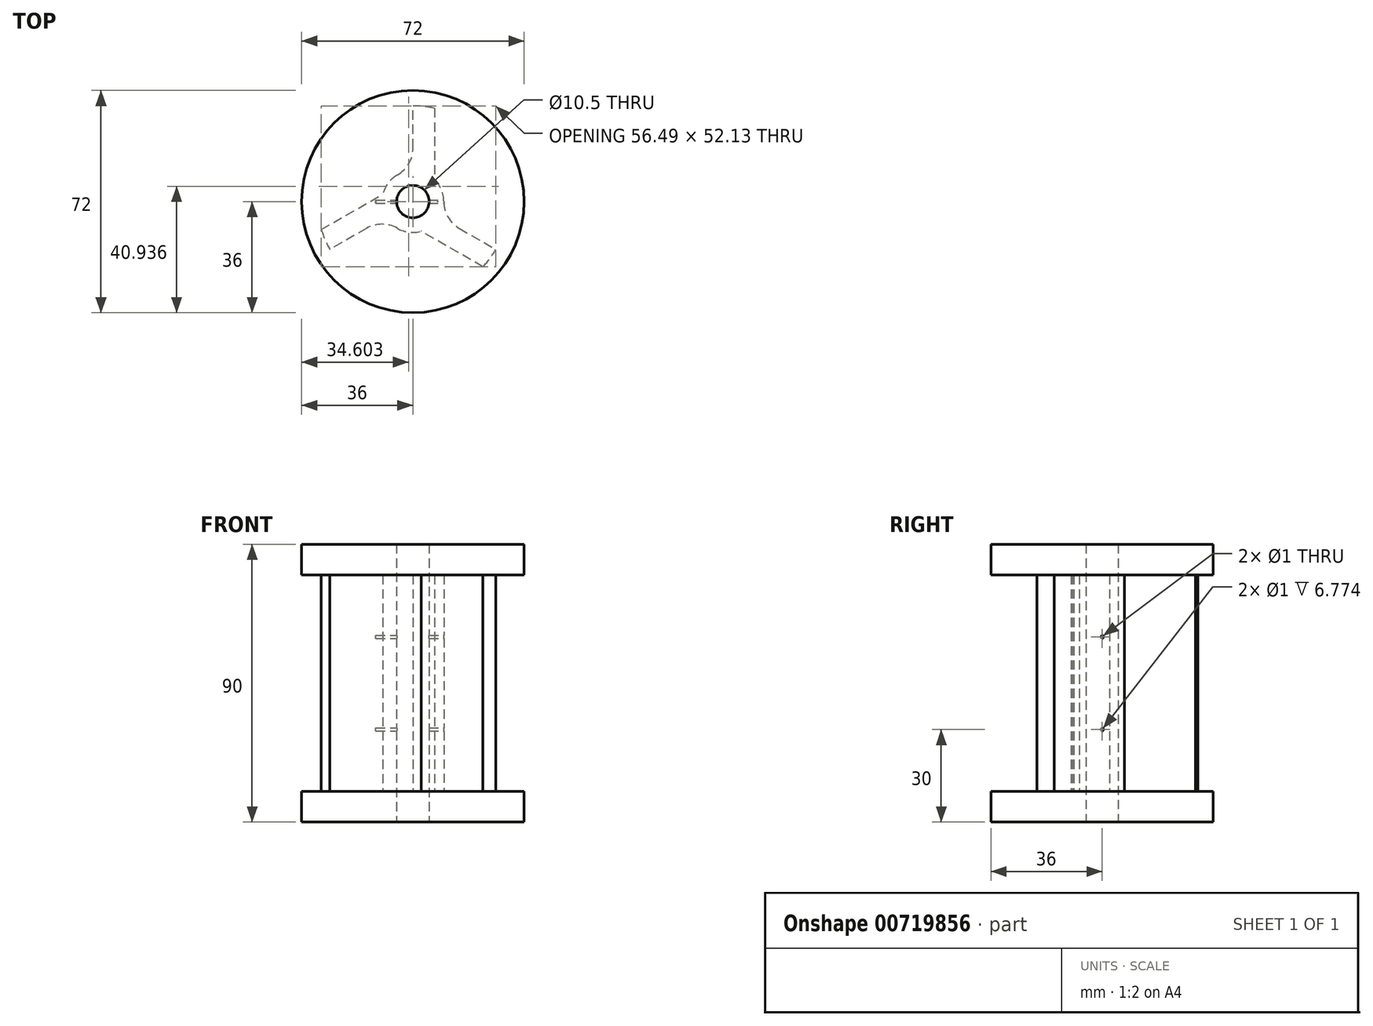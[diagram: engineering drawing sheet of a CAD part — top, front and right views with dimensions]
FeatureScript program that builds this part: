
annotation { "Feature Type Name" : "Feature", "Feature Type Description" : "" }
export const myFeature = defineFeature(function(context is Context, id is Id, definition is map)
    precondition{}
    {
        {
            var Q0;
            Q0=qCreatedBy(makeId("Top.planeOp"),FACE);
            var sketch = newSketch(context, id + "F0", { "sketchPlane" : qUnion([Q0])});
            skCircle(sketch, "E0", {"center": v(0, 0) * mm, "radius": 31 * mm});
            skCircle(sketch, "E1", {"center": v(0, 0) * mm, "radius": 5.25 * mm});
            skCircle(sketch, "E2", {"center": v(0, 0) * mm, "radius": 10 * mm});
            skLineSegment(sketch, "E3", {"start": v(0, 0) * mm, "end": v(-26.85, -15.5) * mm});
            skLineSegment(sketch, "E4", {"start": v(0, 0) * mm, "end": v(0, 31) * mm});
            skLineSegment(sketch, "E5", {"start": v(0, 0) * mm, "end": v(26.85, -15.5) * mm});
            skLineSegment(sketch, "E6", {"start": v(0, 0) * mm, "end": v(-29.64, -9.08) * mm});
            skLineSegment(sketch, "E7", {"start": v(-29.64, -9.08) * mm, "end": v(-9.7, 2.43) * mm});
            skLineSegment(sketch, "E8", {"start": v(0, 0) * mm, "end": v(6.96, 30.2) * mm});
            skLineSegment(sketch, "E9", {"start": v(6.96, 30.2) * mm, "end": v(6.96, 7.19) * mm});
            skLineSegment(sketch, "E10", {"start": v(0, 0) * mm, "end": v(22.68, -21.13) * mm});
            skLineSegment(sketch, "E11", {"start": v(22.68, -21.13) * mm, "end": v(2.74, -9.62) * mm});
            skSolve(sketch);
        }
        {
            var Q0;
            {var subQ3=sQuery(id+"F0.wireOp",EDGE,"E10");var subQ5=sQuery(id+"F0.wireOp",EDGE,"E2");var subQ6=makeQuery(id+"F0.imprint","INTERSECT",VERTEX,{"derivedFrom":[subQ5,subQ3]});Q0=makeQuery(id+"F0.imprint","IMPRINT",FACE,{"disambiguationData":[TD([[makeQuery(id+"F0.imprint","IMPRINT",EDGE,{"disambiguationData":[TD([[subQ6,-1.0]])],"derivedFrom":subQ5}),-1.0]])]});}
            var Q1;
            {var subQ0=sQuery(id+"F0.wireOp",EDGE,"E11");Q1=makeQuery(id+"F0.imprint","IMPRINT",FACE,{"disambiguationData":[TD([[makeQuery(id+"F0.imprint","IMPRINT",EDGE,{"derivedFrom":subQ0}),-1.0]])]});}
            var Q2;
            {var subQ4=sQuery(id+"F0.wireOp",EDGE,"E3");var subQ5=sQuery(id+"F0.wireOp",EDGE,"E1");var subQ6=makeQuery(id+"F0.imprint","INTERSECT",VERTEX,{"derivedFrom":[subQ5,subQ4]});Q2=makeQuery(id+"F0.imprint","IMPRINT",FACE,{"disambiguationData":[TD([[makeQuery(id+"F0.imprint","IMPRINT",EDGE,{"disambiguationData":[TD([[subQ6,-1.0]])],"derivedFrom":subQ5}),-1.0]])]});}
            var Q3;
            {var subQ0=sQuery(id+"F0.wireOp",EDGE,"E10");var subQ1=sQuery(id+"F0.wireOp",EDGE,"E1");var subQ2=makeQuery(id+"F0.imprint","INTERSECT",VERTEX,{"derivedFrom":[subQ1,subQ0]});Q3=makeQuery(id+"F0.imprint","IMPRINT",FACE,{"disambiguationData":[TD([[makeQuery(id+"F0.imprint","IMPRINT",EDGE,{"disambiguationData":[TD([[subQ2,-1.0]])],"derivedFrom":subQ1}),-1.0]])]});}
            var Q4;
            {var subQ1=sQuery(id+"F0.wireOp",EDGE,"E1");var subQ6=sQuery(id+"F0.wireOp",EDGE,"E8");var subQ8=makeQuery(id+"F0.imprint","INTERSECT",VERTEX,{"derivedFrom":[subQ1,subQ6]});Q4=makeQuery(id+"F0.imprint","IMPRINT",FACE,{"disambiguationData":[TD([[makeQuery(id+"F0.imprint","IMPRINT",EDGE,{"disambiguationData":[TD([[subQ8,1.0]])],"derivedFrom":subQ1}),-1.0]])]});}
            var Q5;
            {var subQ0=sQuery(id+"F0.wireOp",EDGE,"E4");var subQ1=sQuery(id+"F0.wireOp",EDGE,"E1");var subQ2=makeQuery(id+"F0.imprint","INTERSECT",VERTEX,{"derivedFrom":[subQ1,subQ0]});Q5=makeQuery(id+"F0.imprint","IMPRINT",FACE,{"disambiguationData":[TD([[makeQuery(id+"F0.imprint","IMPRINT",EDGE,{"disambiguationData":[TD([[subQ2,-1.0]])],"derivedFrom":subQ1}),-1.0]])]});}
            var Q6;
            {var subQ0=sQuery(id+"F0.wireOp",EDGE,"E4");var subQ1=sQuery(id+"F0.wireOp",EDGE,"E1");var subQ2=makeQuery(id+"F0.imprint","INTERSECT",VERTEX,{"derivedFrom":[subQ1,subQ0]});Q6=makeQuery(id+"F0.imprint","IMPRINT",FACE,{"disambiguationData":[TD([[makeQuery(id+"F0.imprint","IMPRINT",EDGE,{"disambiguationData":[TD([[subQ2,1.0]])],"derivedFrom":subQ1}),-1.0]])]});}
            var Q7;
            {var subQ0=sQuery(id+"F0.wireOp",EDGE,"E6");var subQ1=sQuery(id+"F0.wireOp",EDGE,"E1");var subQ2=makeQuery(id+"F0.imprint","INTERSECT",VERTEX,{"derivedFrom":[subQ1,subQ0]});Q7=makeQuery(id+"F0.imprint","IMPRINT",FACE,{"disambiguationData":[TD([[makeQuery(id+"F0.imprint","IMPRINT",EDGE,{"disambiguationData":[TD([[subQ2,-1.0]])],"derivedFrom":subQ1}),-1.0]])]});}
            var Q8;
            {var subQ0=sQuery(id+"F0.wireOp",EDGE,"E9");Q8=makeQuery(id+"F0.imprint","IMPRINT",FACE,{"disambiguationData":[TD([[makeQuery(id+"F0.imprint","IMPRINT",EDGE,{"derivedFrom":subQ0}),-1.0]])]});}
            var Q9;
            {var subQ3=sQuery(id+"F0.wireOp",EDGE,"E8");var subQ5=sQuery(id+"F0.wireOp",EDGE,"E2");var subQ6=makeQuery(id+"F0.imprint","INTERSECT",VERTEX,{"derivedFrom":[subQ5,subQ3]});Q9=makeQuery(id+"F0.imprint","IMPRINT",FACE,{"disambiguationData":[TD([[makeQuery(id+"F0.imprint","IMPRINT",EDGE,{"disambiguationData":[TD([[subQ6,-1.0]])],"derivedFrom":subQ5}),-1.0]])]});}
            var Q10;
            {var subQ0=sQuery(id+"F0.wireOp",EDGE,"E7");Q10=makeQuery(id+"F0.imprint","IMPRINT",FACE,{"disambiguationData":[TD([[makeQuery(id+"F0.imprint","IMPRINT",EDGE,{"derivedFrom":subQ0}),-1.0]])]});}
            var Q11;
            {var subQ3=sQuery(id+"F0.wireOp",EDGE,"E6");var subQ5=sQuery(id+"F0.wireOp",EDGE,"E2");var subQ6=makeQuery(id+"F0.imprint","INTERSECT",VERTEX,{"derivedFrom":[subQ5,subQ3]});Q11=makeQuery(id+"F0.imprint","IMPRINT",FACE,{"disambiguationData":[TD([[makeQuery(id+"F0.imprint","IMPRINT",EDGE,{"disambiguationData":[TD([[subQ6,-1.0]])],"derivedFrom":subQ5}),-1.0]])]});}
            extrude(context, id + "F1", {"entities" : qUnion([Q0, Q1, Q2, Q3, Q4, Q5, Q6, Q7, Q8, Q9, Q10, Q11]), "depth" : 75 * mm, "offsetDistance" : 25 * mm});
        }
        {
            var Q0;
            Q0=qCreatedBy(makeId("Top.planeOp"),FACE);
            var sketch = newSketch(context, id + "F2", { "sketchPlane" : qUnion([Q0])});
            skCircle(sketch, "E12", {"center": v(0, 0) * mm, "radius": 36 * mm});
            skCircle(sketch, "E13", {"center": v(0, 0) * mm, "radius": 5.25 * mm});
            skSolve(sketch);
        }
        {
            var Q0;
            Q0=makeQuery(id+"F2.imprint","IMPRINT",FACE,{"disambiguationData":[TD([[makeQuery(id+"F2.imprint","IMPRINT",EDGE,{"derivedFrom":sQuery(id+"F2.wireOp",EDGE,"E12")}),1.0]])]});
            extrude(context, id + "F3", {"entities" : qUnion([Q0]), "operationType" : NewBodyOperationType.ADD, "oppositeDirection" : true, "depth" : 10 * mm, "offsetDistance" : 25 * mm});
        }
        {
            var Q0;
            Q0=makeQuery(id+"F1.opExtrude","SWEPT_EDGE",EDGE,{"disambiguationData":[OSD([sQuery(id+"F0.wireOp",EDGE,"E2"),sQuery(id+"F0.wireOp",EDGE,"E3")])]});
            var Q1;
            Q1=makeQuery(id+"F1.opExtrude","SWEPT_EDGE",EDGE,{"disambiguationData":[OSD([sQuery(id+"F0.wireOp",EDGE,"E2"),sQuery(id+"F0.wireOp",EDGE,"E5")])]});
            var Q2;
            Q2=makeQuery(id+"F1.opExtrude","SWEPT_EDGE",EDGE,{"disambiguationData":[OSD([sQuery(id+"F0.wireOp",EDGE,"E2"),sQuery(id+"F0.wireOp",EDGE,"E4")])]});
            fillet(context, id + "F4", {"entities" : qUnion([Q0, Q1, Q2]), "radius" : 10 * mm, "tangentPropagation" : true, "allowEdgeOverflow" : false});
        }
        {
            var Q0;
            Q0=qCreatedBy(makeId("Right.planeOp"),FACE);
            var sketch = newSketch(context, id + "F5", { "sketchPlane" : qUnion([Q0])});
            skPoint(sketch, "E14", {"position": v(0, 0) * mm});
            skPoint(sketch, "E15", {"position": v(0, 50) * mm});
            skPoint(sketch, "E16", {"position": v(0, 20) * mm});
            skCircle(sketch, "E17", {"center": v(0, 50) * mm, "radius": 0.5 * mm});
            skCircle(sketch, "E18", {"center": v(0, 20) * mm, "radius": 0.5 * mm});
            skSolve(sketch);
        }
        {
            var Q0;
            Q0=makeQuery(id+"F5.imprint","IMPRINT",FACE,{"disambiguationData":[TD([[makeQuery(id+"F5.imprint","IMPRINT",EDGE,{"derivedFrom":sQuery(id+"F5.wireOp",EDGE,"E17")}),1.0]])]});
            var Q1;
            Q1=makeQuery(id+"F5.imprint","IMPRINT",FACE,{"disambiguationData":[TD([[makeQuery(id+"F5.imprint","IMPRINT",EDGE,{"derivedFrom":sQuery(id+"F5.wireOp",EDGE,"E18")}),1.0]])]});
            extrude(context, id + "F6", {"entities" : qUnion([Q0, Q1]), "operationType" : NewBodyOperationType.REMOVE, "oppositeDirection" : true, "depth" : 12 * mm, "offsetDistance" : 25 * mm, "hasSecondDirection" : true, "secondDirectionOppositeDirection" : false, "secondDirectionDepth" : 11 * mm});
        }
        {
            var Q0;
            Q0=makeQuery(id+"F1.opExtrude","CAP_FACE",FACE,{"disambiguationData":[OSD([sQuery(id+"F0.wireOp",EDGE,"E0"),sQuery(id+"F0.wireOp",EDGE,"E1"),sQuery(id+"F0.wireOp",EDGE,"E2"),sQuery(id+"F0.wireOp",EDGE,"E3"),sQuery(id+"F0.wireOp",EDGE,"E4"),sQuery(id+"F0.wireOp",EDGE,"E5"),sQuery(id+"F0.wireOp",EDGE,"E7"),sQuery(id+"F0.wireOp",EDGE,"E9"),sQuery(id+"F0.wireOp",EDGE,"E11")])],"isStart":false});
            var sketch = newSketch(context, id + "F7", { "sketchPlane" : qUnion([Q0])});
            skCircle(sketch, "E19", {"center": v(0, 0) * mm, "radius": 36 * mm});
            skSolve(sketch);
        }
        {
            var Q0;
            {var subQ0=sQuery(id+"F0.wireOp",EDGE,"E7");var subQ3=makeQuery(id+"F1.opExtrude","CAP_EDGE",EDGE,{"disambiguationData":[OSD([subQ0])],"isStart":false});Q0=makeQuery(id+"F7.imprint","IMPRINT",FACE,{"disambiguationData":[TD([[makeQuery(id+"F7.imprint","IMPRINT",EDGE,{"derivedFrom":subQ3}),1.0]])]});}
            var Q1;
            {var subQ7=sQuery(id+"F0.wireOp",EDGE,"E1");Q1=makeQuery(id+"F7.imprint","IMPRINT",FACE,{"disambiguationData":[TD([[makeQuery(id+"F7.imprint","IMPRINT",EDGE,{"derivedFrom":makeQuery(id+"F1.opExtrude","CAP_EDGE",EDGE,{"disambiguationData":[OSD([subQ7])],"isStart":false})}),-1.0]])]});}
            var Q2;
            {var subQ0=sQuery(id+"F0.wireOp",EDGE,"E11");var subQ5=makeQuery(id+"F1.opExtrude","CAP_EDGE",EDGE,{"disambiguationData":[OSD([subQ0])],"isStart":false});Q2=makeQuery(id+"F7.imprint","IMPRINT",FACE,{"disambiguationData":[TD([[makeQuery(id+"F7.imprint","IMPRINT",EDGE,{"derivedFrom":subQ5}),1.0]])]});}
            var Q3;
            {var subQ0=sQuery(id+"F0.wireOp",EDGE,"E9");var subQ3=makeQuery(id+"F1.opExtrude","CAP_EDGE",EDGE,{"disambiguationData":[OSD([subQ0])],"isStart":false});Q3=makeQuery(id+"F7.imprint","IMPRINT",FACE,{"disambiguationData":[TD([[makeQuery(id+"F7.imprint","IMPRINT",EDGE,{"derivedFrom":subQ3}),1.0]])]});}
            extrude(context, id + "F8", {"entities" : qUnion([Q0, Q1, Q2, Q3]), "depth" : 5 * mm, "offsetDistance" : 25 * mm});
        }
        {
            var Q0;
            {var subQ0=sQuery(id+"F0.wireOp",EDGE,"E11");var subQ5=makeQuery(id+"F1.opExtrude","CAP_EDGE",EDGE,{"disambiguationData":[OSD([subQ0])],"isStart":false});Q0=makeQuery(id+"F7.imprint","IMPRINT",FACE,{"disambiguationData":[TD([[makeQuery(id+"F7.imprint","IMPRINT",EDGE,{"derivedFrom":subQ5}),1.0]])]});}
            var Q1;
            {var subQ0=sQuery(id+"F0.wireOp",EDGE,"E9");var subQ3=makeQuery(id+"F1.opExtrude","CAP_EDGE",EDGE,{"disambiguationData":[OSD([subQ0])],"isStart":false});Q1=makeQuery(id+"F7.imprint","IMPRINT",FACE,{"disambiguationData":[TD([[makeQuery(id+"F7.imprint","IMPRINT",EDGE,{"derivedFrom":subQ3}),1.0]])]});}
            var Q2;
            {var subQ0=sQuery(id+"F0.wireOp",EDGE,"E7");var subQ3=makeQuery(id+"F1.opExtrude","CAP_EDGE",EDGE,{"disambiguationData":[OSD([subQ0])],"isStart":false});Q2=makeQuery(id+"F7.imprint","IMPRINT",FACE,{"disambiguationData":[TD([[makeQuery(id+"F7.imprint","IMPRINT",EDGE,{"derivedFrom":subQ3}),1.0]])]});}
            extrude(context, id + "F9", {"entities" : qUnion([Q0, Q1, Q2]), "operationType" : NewBodyOperationType.ADD, "oppositeDirection" : true, "depth" : 5 * mm, "offsetDistance" : 25 * mm});
        }
    });
